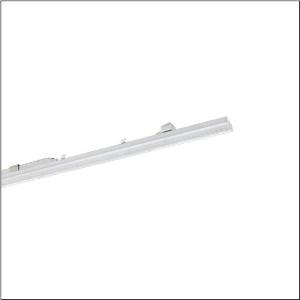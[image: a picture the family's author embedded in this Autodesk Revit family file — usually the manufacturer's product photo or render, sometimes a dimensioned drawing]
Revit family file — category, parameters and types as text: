
# Revit family: tl_l_5wd7a8d0h2c5
name_source: partatom
category: Lighting Fixtures
units: mm (PartAtom-declared; Revit-internal decimal feet)

## family parameters
Cut with Voids When Loaded = No
Host = Face
Light Source = No
Part Type = Normal
Room Calculation Point = No
Round Connector Dimension = Use Diameter
Shared = No

## types (1)
- --- (1 x LED, 9800 lm, 63.3 W, 4000K)
    Apparent Load = 63 VA
    CIE Flux Codes = 49 84 98 100 100
    Color Rendering = 80
    Color Temperature = 4000K
    Default Elevation = 1800 mm
    Description = TL L, luminaire insert, of sheet steel, galvanised, coil coated, white, length: 1.500mm, width: 66mm, height: 67mm, surge protection,LED rated luminous flux: 9.800lm, light colour: 840, control gear: DALI, with terminal, 5-pole, mains connection: 230..240V, AC, 50/60Hz, rated input power: 63W, micro fuse,primary optical cover: cover, of PMMA, light emission: direct distribution, protection rating (complete): as luminaire, insulation class (complete): insulation class I (protective earthing), certification: CE, impact resistance: IK06, permissible ambient temperature for indoor applications: -25..+35°C, packaging unit: 1 piece
    Height = 120 mm
    Lamp = 1 x LED
    Lamp Light Flux = 9800 lm
    Lamp Power = 63.3 W
    Lamp count = 1
    Length = 1690 mm
    Luminous efficacy = 155 lm/W
    Manufacturer = Siteco
    ModVariant = No
    Model = 5WD7A8D0H2C5
    Mounting Place = Ceiling
    Mounting Type = Pendant
    Number of Poles = 1
    OnlyDefault = Yes
    Power Factor = 1
    Product Name = TL L
    Product group = luminaire insert
    ProductGroupID = 901
    Protection Class = Protection class I
    Protection Degree = Degree of protection
    RLX_Detail_Level = 1
    RLX_Emergency_Light_Flux = 0 lm
    RLX_Emergency_Type = 0
    RLX_Emergency_Type_DB = No
    RlxData = <blob elided: 17345 chars, md5=51337cae>
    Socket = socket
    Standby Power = 0 W
    System Light Flux = 9800 lm
    System Power = 63 W
    Type Comments = factory setting: luminous flux: 100 % | dim-lin: 254 | 420 mA
    Type Image = l_1294382.jpg
    URL = http://relux.com
    VarID = @adj_012363
    Voltage = 0 V
    Weight = 0.00 kg
    Width = 208 mm

## geometry (parser evidence)
native form markers: Blend x4, Sweep x10
no freeform markers — native parametric forms only
